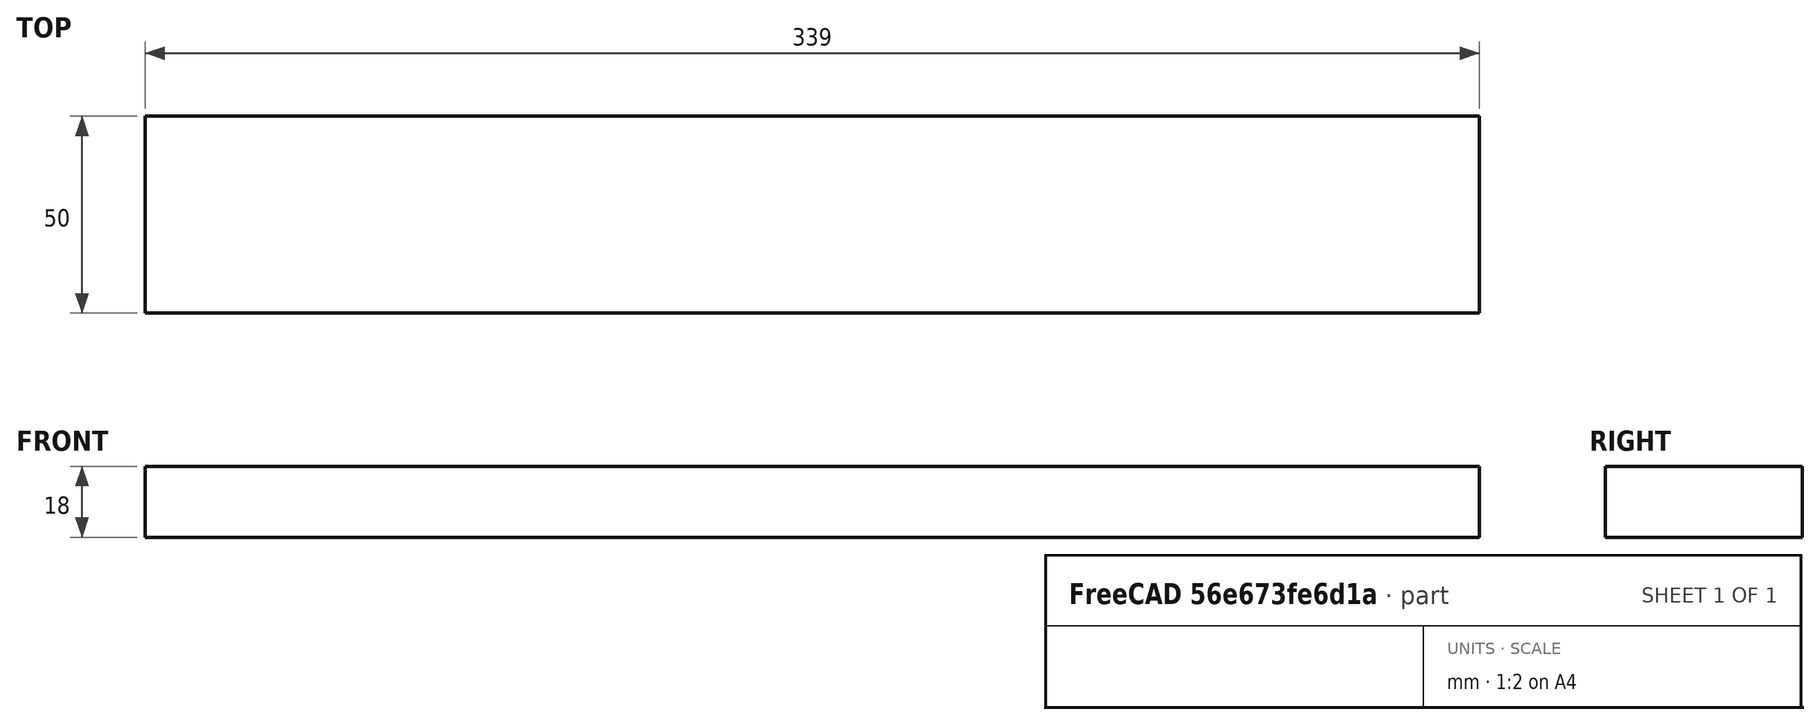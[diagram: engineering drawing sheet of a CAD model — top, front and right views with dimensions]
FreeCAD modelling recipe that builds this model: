
FCSTD DOCUMENT  (FreeCAD 1.0R39109 (Git))
Label: 82_base_sides
License: All rights reserved
LicenseURL: http://en.wikipedia.org/wiki/All_rights_reserved
objects: Spreadsheet::Sheet×1, Sketcher::SketchObject×1, PartDesign::Pad×1, PartDesign::Body×1
note: 6 computed .brp shape members not serialized (recipe doc carries the construction recipe); baked Part::Feature solids carry a one-line shape summary decoded from their .brp

FEATURE [Spreadsheet::Sheet] Spreadsheet
  cells = A2='length; B2(length)=339; A3='width; B3(width)=50; A4='height; B4(height)=18
FEATURE [Sketcher::SketchObject] Sketch
  ArcFitTolerance = 0
  AttachmentSupport = -> [XY_Plane]
  FullyConstrained = true
  MakeInternals = false
  MapMode = 5
  expr: Constraints[11] = Spreadsheet.length
  expr: Constraints[12] = Spreadsheet.width
  sketch-geometry (5):
    g0: LineSegment StartX=-169.5 StartY=25 StartZ=0 EndX=169.5 EndY=25 EndZ=0
    g1: LineSegment StartX=169.5 StartY=25 StartZ=0 EndX=169.5 EndY=-25 EndZ=0
    g2: LineSegment StartX=169.5 StartY=-25 StartZ=0 EndX=-169.5 EndY=-25 EndZ=0
    g3: LineSegment StartX=-169.5 StartY=-25 StartZ=0 EndX=-169.5 EndY=25 EndZ=0
    g4: LineSegment [constr] StartX=-169.5 StartY=25 StartZ=0 EndX=169.5 EndY=-25 EndZ=0
  constraints (13):
    c: Coincident(g0,g1)
    c: Coincident(g1,g2)
    c: Coincident(g2,g3)
    c: Coincident(g3,g0)
    c: Horizontal(g0)
    c: Horizontal(g2)
    c: Vertical(g1)
    c: Vertical(g3)
    c: Coincident(g4,g1)
    c: Coincident(g0,g4)
    c: Symmetric(g0,g1,g-1)
    c: Distance(g0,g0) = 339
    c: Distance(g0,g2) = 50
FEATURE [PartDesign::Pad] Pad
  Direction = (0,0,1)
  Length = 18
  Length2 = 10
  Profile = -> Sketch
  ReferenceAxis = -> Sketch [N_Axis]
  Suppressed = false
  Type = 0
  expr: Length = Spreadsheet.height
FEATURE [PartDesign::Body] Body
  AllowCompound = false
  Group = -> [Sketch,Pad]
  Origin = -> Origin
  Tip = -> Pad
